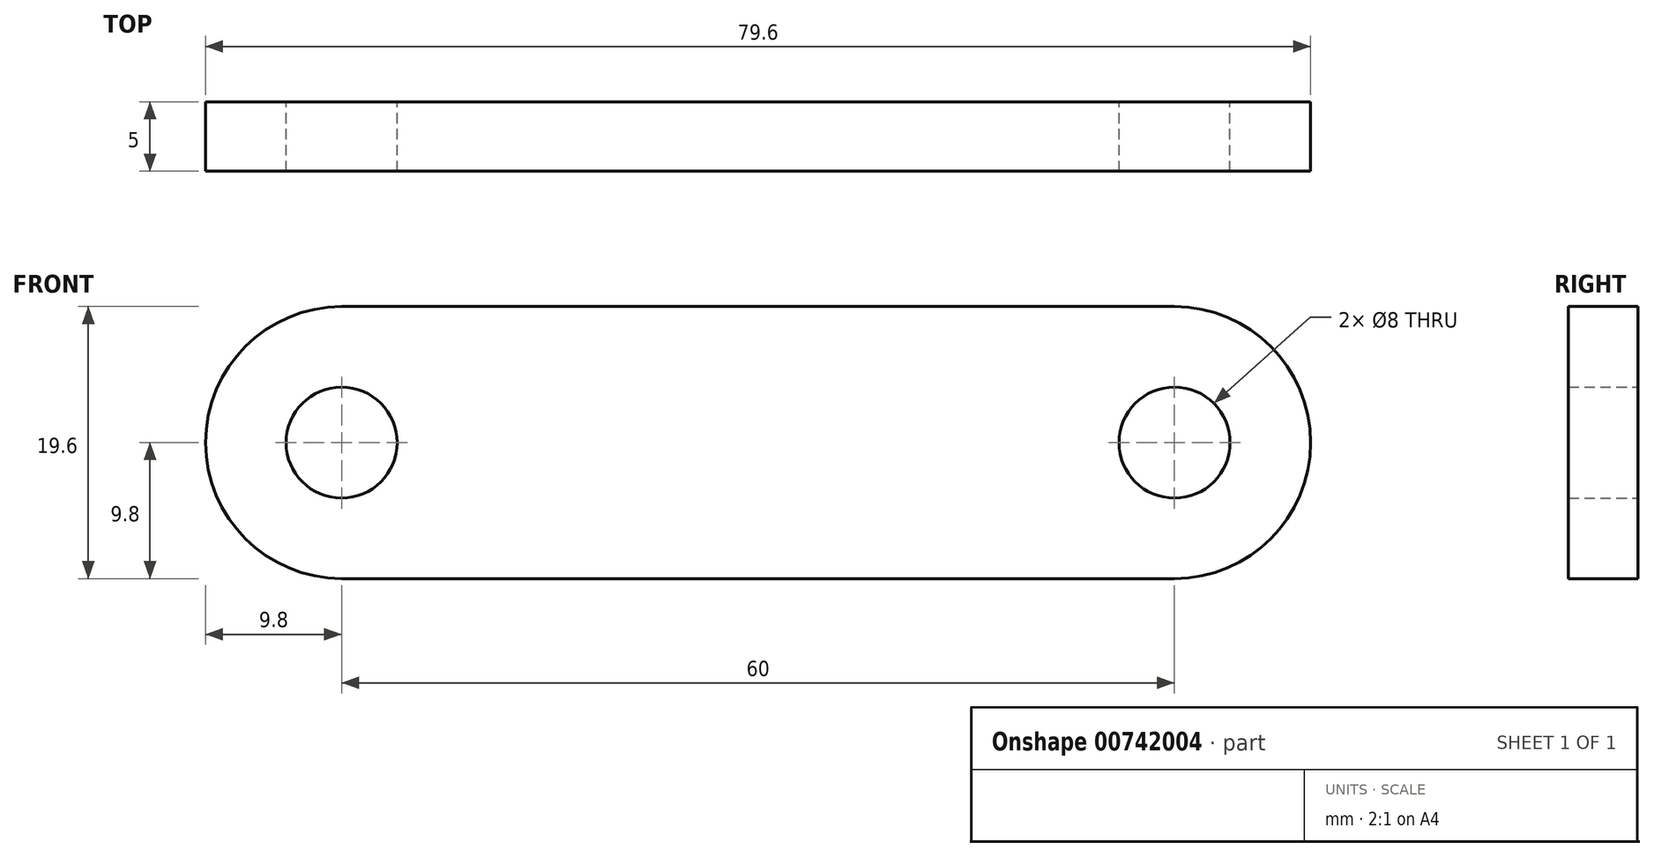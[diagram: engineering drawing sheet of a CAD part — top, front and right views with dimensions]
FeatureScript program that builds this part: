
annotation { "Feature Type Name" : "Feature", "Feature Type Description" : "" }
export const myFeature = defineFeature(function(context is Context, id is Id, definition is map)
    precondition{}
    {
        {
            var Q0;
            Q0=qCreatedBy(makeId("Front.planeOp"),FACE);
            var sketch = newSketch(context, id + "F0", { "sketchPlane" : qUnion([Q0])});
            skLineSegment(sketch, "E0", {"start": v(-56.78, 0) * mm, "end": v(69.4, 0) * mm, "construction": true});
            skLineSegment(sketch, "E1", {"start": v(0, -49.44) * mm, "end": v(0, 55.1) * mm, "construction": true});
            skLineSegment(sketch, "E2", {"start": v(0, 9.8) * mm, "end": v(-30, 9.8) * mm});
            skLineSegment(sketch, "E3.MirrorCS", {"start": v(0, -9.8) * mm, "end": v(-30, -9.8) * mm});
            skArc(sketch, "E4", {"start": v(-30, 9.8) * mm, "mid": v(-39.8, 0) * mm, "end": v(-30, -9.8) * mm});
            skCircle(sketch, "E5", {"center": v(-30, 0) * mm, "radius": 4 * mm});
            skLineSegment(sketch, "E6.MirrorCS", {"start": v(0, 9.8) * mm, "end": v(30, 9.8) * mm});
            skLineSegment(sketch, "E7.MirrorCS", {"start": v(0, -9.8) * mm, "end": v(30, -9.8) * mm});
            skArc(sketch, "E8.MirrorCS", {"start": v(30, 9.8) * mm, "mid": v(39.8, 0) * mm, "end": v(30, -9.8) * mm});
            skCircle(sketch, "E9.MirrorC", {"center": v(30, 0) * mm, "radius": 4 * mm});
            skSolve(sketch);
        }
        {
            var Q0;
            Q0 = qSketchRegion(id + "F0", true);
            extrude(context, id + "F1", {"entities" : qUnion([Q0]), "endBound" : BoundingType.SYMMETRIC, "depth" : 5 * mm, "offsetDistance" : 25.4 * mm});
        }
    });
